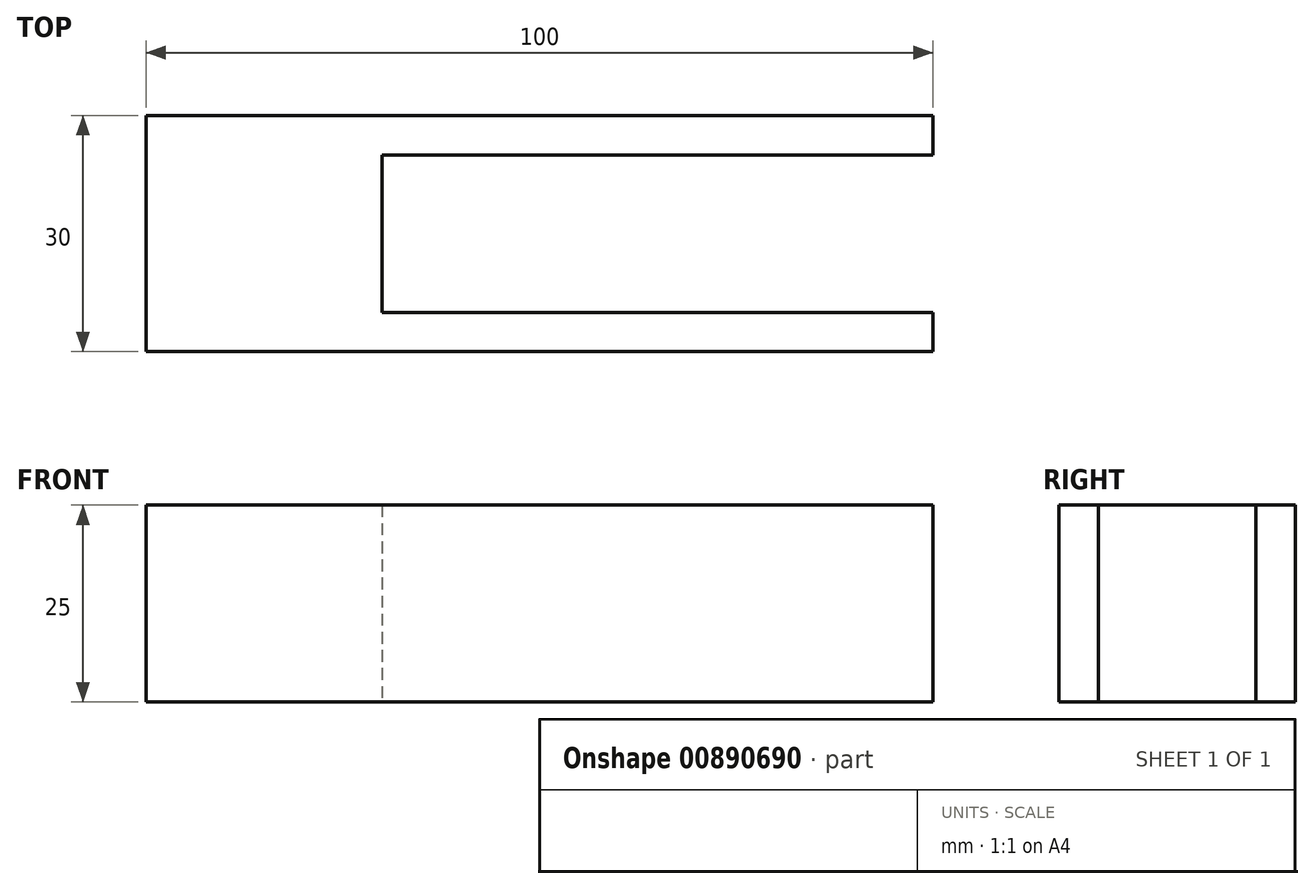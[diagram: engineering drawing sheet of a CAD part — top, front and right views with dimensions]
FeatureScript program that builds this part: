
annotation { "Feature Type Name" : "Feature", "Feature Type Description" : "" }
export const myFeature = defineFeature(function(context is Context, id is Id, definition is map)
    precondition{}
    {
        {
            var Q0;
            Q0=qCreatedBy(makeId("Top.planeOp"),FACE);
            var sketch = newSketch(context, id + "F0", { "sketchPlane" : qUnion([Q0])});
            skLineSegment(sketch, "E0", {"start": v(35.11, 2.26) * mm, "end": v(-64.89, 2.26) * mm});
            skLineSegment(sketch, "E1", {"start": v(-64.89, 2.26) * mm, "end": v(-64.89, -27.74) * mm});
            skLineSegment(sketch, "E2", {"start": v(-64.89, -27.74) * mm, "end": v(35.11, -27.74) * mm});
            skLineSegment(sketch, "E3", {"start": v(35.11, -27.74) * mm, "end": v(35.11, -22.74) * mm});
            skLineSegment(sketch, "E4", {"start": v(35.11, -22.74) * mm, "end": v(-34.89, -22.74) * mm});
            skLineSegment(sketch, "E5", {"start": v(35.11, -2.74) * mm, "end": v(35.11, 2.26) * mm});
            skLineSegment(sketch, "E6", {"start": v(35.11, -2.74) * mm, "end": v(-34.89, -2.74) * mm});
            skLineSegment(sketch, "E7", {"start": v(-34.89, -2.74) * mm, "end": v(-34.89, -22.74) * mm});
            skPoint(sketch, "E8.orphan", {"position": v(-64.89, -22.74) * mm});
            skPoint(sketch, "E9.orphan", {"position": v(-64.89, -2.74) * mm});
            skSolve(sketch);
        }
        {
            var Q0;
            Q0 = qSketchRegion(id + "F0", true);
            extrude(context, id + "F1", {"entities" : qUnion([Q0]), "depth" : 25 * mm, "offsetDistance" : 25 * mm});
        }
    });
